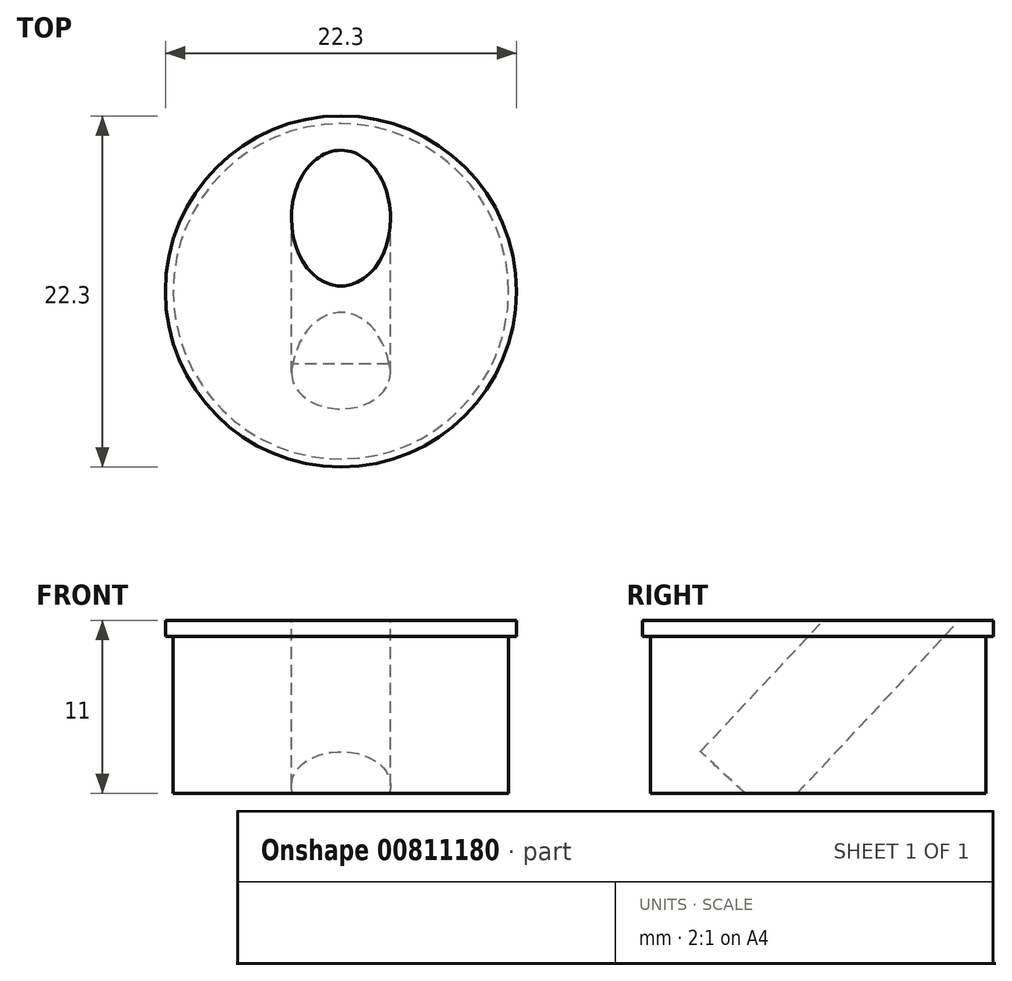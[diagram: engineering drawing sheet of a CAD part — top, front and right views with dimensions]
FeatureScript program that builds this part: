
annotation { "Feature Type Name" : "Feature", "Feature Type Description" : "" }
export const myFeature = defineFeature(function(context is Context, id is Id, definition is map)
    precondition{}
    {
        {
            var Q0;
            Q0=qCreatedBy(makeId("Top.planeOp"),FACE);
            var sketch = newSketch(context, id + "F0", { "sketchPlane" : qUnion([Q0])});
            skCircle(sketch, "E0", {"center": v(0, 0) * mm, "radius": 10.65 * mm});
            skSolve(sketch);
        }
        {
            var Q0;
            Q0=qSketchRegion(id+"F0",true);
            extrude(context, id + "F1", {"entities" : qUnion([Q0]), "depth" : 10 * mm, "offsetDistance" : 25 * mm});
        }
        {
            var Q0;
            Q0=makeQuery(id+"F1.opExtrude","CAP_FACE",FACE,{"disambiguationData":[OSD([sQuery(id+"F0.wireOp",EDGE,"E0")])],"isStart":false});
            var sketch = newSketch(context, id + "F2", { "sketchPlane" : qUnion([Q0])});
            skCircle(sketch, "E1", {"center": v(0, 0) * mm, "radius": 11.15 * mm});
            skCircle(sketch, "E2.0", {"center": v(0, 0) * mm, "radius": 10.65 * mm, "construction": true});
            skSolve(sketch);
        }
        {
            var Q0;
            Q0=makeQuery(id+"F2.imprint","IMPRINT",FACE,{"disambiguationData":[TD([[makeQuery(id+"F2.imprint","IMPRINT",EDGE,{"derivedFrom":sQuery(id+"F2.wireOp",EDGE,"E1")}),1.0]])]});
            var Q1;
            Q1=makeQuery(id+"F2.imprint","IMPRINT",FACE,{"disambiguationData":[TD([[makeQuery(id+"F2.imprint","IMPRINT",EDGE,{"derivedFrom":makeQuery(id+"F1.opExtrude","CAP_EDGE",EDGE,{"disambiguationData":[OSD([sQuery(id+"F0.wireOp",EDGE,"E0")])],"isStart":false})}),1.0]])]});
            extrude(context, id + "F3", {"entities" : qUnion([Q0, Q1]), "operationType" : NewBodyOperationType.ADD, "depth" : 1 * mm, "offsetDistance" : 25 * mm});
        }
        {
            var Q0;
            Q0=makeQuery(id+"F1.opExtrude","CAP_FACE",FACE,{"disambiguationData":[OSD([sQuery(id+"F0.wireOp",EDGE,"E0")])],"isStart":true});
            var sketch = newSketch(context, id + "F4", { "sketchPlane" : qUnion([Q0])});
            skPoint(sketch, "E3", {"position": v(0, 5.65) * mm});
            skSolve(sketch);
        }
        {
            var Q0;
            Q0=qCreatedBy(makeId("Right.planeOp"),FACE);
            var sketch = newSketch(context, id + "F5", { "sketchPlane" : qUnion([Q0])});
            skPoint(sketch, "E4.0", {"position": v(-5.65, 0) * mm});
            skPoint(sketch, "E5.0", {"position": v(4.65, 11) * mm});
            skLineSegment(sketch, "E6", {"start": v(-5.65, 0) * mm, "end": v(13.68, 20.64) * mm});
            skLineSegment(sketch, "E7.0", {"start": v(-10.65, 11) * mm, "end": v(10.65, 11) * mm, "construction": true});
            skSolve(sketch);
        }
        {
            var Q0;
            Q0=sQuery(id+"F5.wireOp",EDGE,"E6");
            var Q1;
            Q1=sQuery(id+"F5.wireOp",VERTEX,"E6.end");
            cPlane(context, id + "F6", {"entities" : qUnion([Q0, Q1]), "cplaneType" : CPlaneType.LINE_POINT, "offset" : 25 * mm, "width" : 150 * mm, "height" : 150 * mm});
        }
        {
            var Q0;
            Q0=qCreatedBy(id+"F6.planeOp",FACE);
            var sketch = newSketch(context, id + "F7", { "sketchPlane" : qUnion([Q0])});
            skPoint(sketch, "E8.0", {"position": v(0, -4.12) * mm});
            skCircle(sketch, "E9", {"center": v(0, -4.12) * mm, "radius": 3.15 * mm});
            skSolve(sketch);
        }
        {
            var Q0;
            Q0=makeQuery(id+"F7.imprint","IMPRINT",FACE,{"disambiguationData":[TD([[makeQuery(id+"F7.imprint","IMPRINT",EDGE,{"derivedFrom":sQuery(id+"F7.wireOp",EDGE,"E9")}),1.0]])]});
            var Q1;
            Q1=makeQuery(id+"F1.opExtrude","CAP_FACE",FACE,{"disambiguationData":[OSD([sQuery(id+"F0.wireOp",EDGE,"E0")])],"isStart":true});
            extrude(context, id + "F8", {"entities" : qUnion([Q0]), "operationType" : NewBodyOperationType.REMOVE, "oppositeDirection" : true, "depth" : 27.57 * mm, "endBoundEntityFace" : qUnion([Q1]), "offsetDistance" : 25 * mm});
        }
    });
